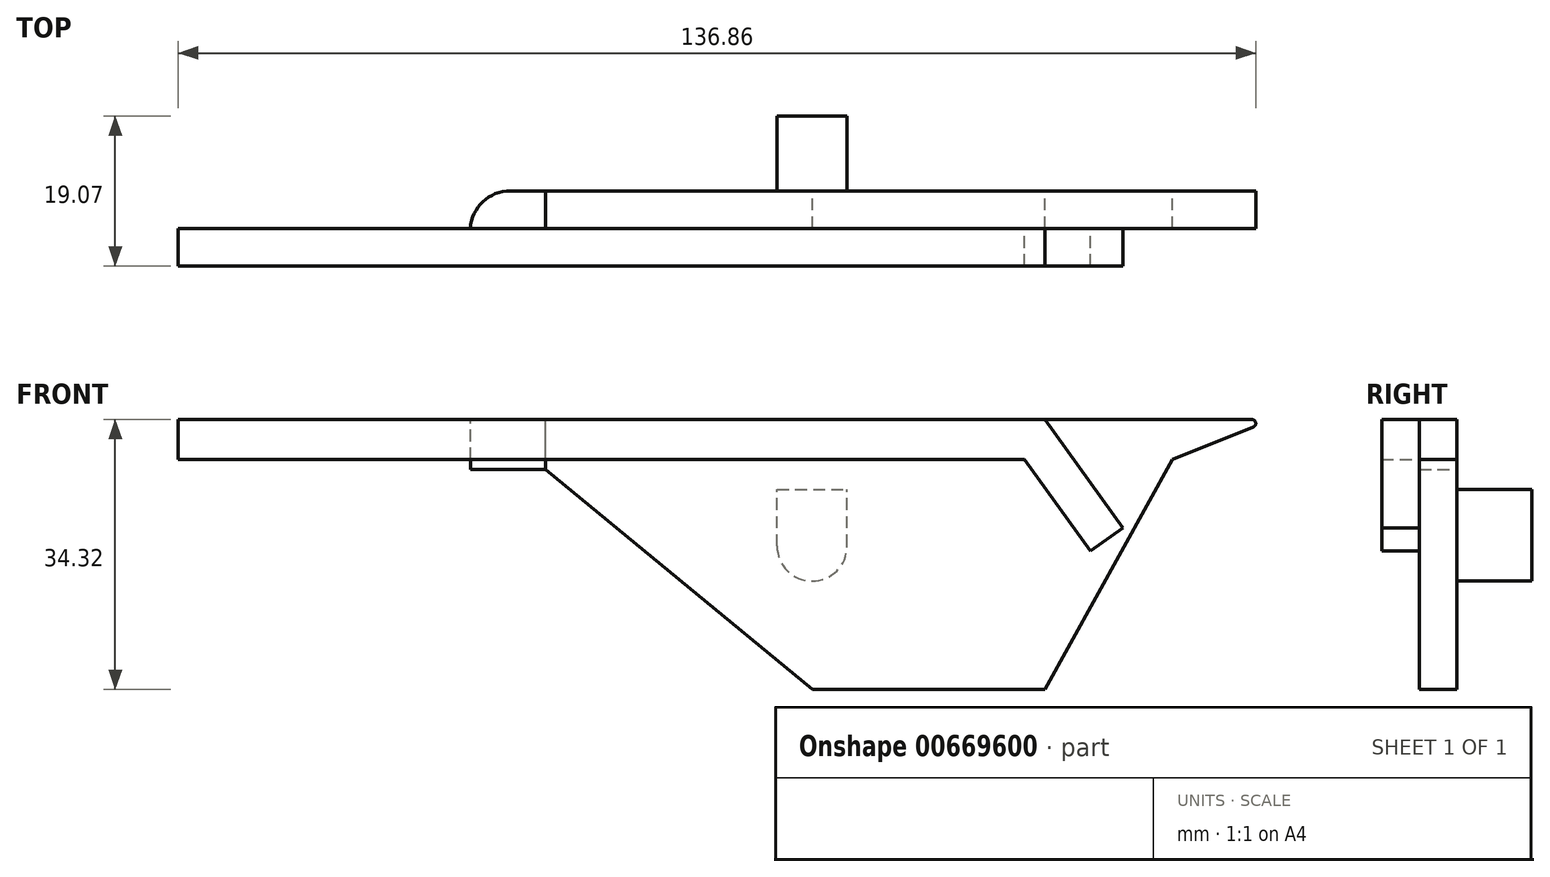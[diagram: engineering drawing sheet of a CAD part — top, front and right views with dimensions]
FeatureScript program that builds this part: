
annotation { "Feature Type Name" : "Feature", "Feature Type Description" : "" }
export const myFeature = defineFeature(function(context is Context, id is Id, definition is map)
    precondition{}
    {
        {
            var Q0;
            Q0=qCreatedBy(makeId("Front.planeOp"),FACE);
            var sketch = newSketch(context, id + "F0", { "sketchPlane" : qUnion([Q0])});
            skLineSegment(sketch, "E0", {"start": v(-28.93, 0) * mm, "end": v(-58.42, 0) * mm});
            skPoint(sketch, "E1.end.orphan", {"position": v(-58.5, 10.16) * mm});
            skPoint(sketch, "E2.end.orphan", {"position": v(-61.98, 10.16) * mm});
            skLineSegment(sketch, "E3", {"start": v(-58.42, 0) * mm, "end": v(-92.38, 27.97) * mm});
            skPoint(sketch, "E4.end.orphan", {"position": v(-68, 0) * mm});
            skLineSegment(sketch, "E5", {"start": v(-92.38, 27.97) * mm, "end": v(-92.38, 34.32) * mm});
            skLineSegment(sketch, "E6", {"start": v(-92.38, 34.32) * mm, "end": v(-28.88, 34.32) * mm});
            skPoint(sketch, "E7.visualSharp", {"position": v(0, 0) * mm});
            skPoint(sketch, "E8.center.orphan", {"position": v(-58.5, 27.97) * mm});
            skLineSegment(sketch, "E9", {"start": v(-2.64, 34.32) * mm, "end": v(-12.73, 34.32) * mm});
            skLineSegment(sketch, "E10", {"start": v(-12.73, 29.24) * mm, "end": v(-2.45, 33.34) * mm});
            skPoint(sketch, "E11.visualSharp", {"position": v(0, 34.32) * mm});
            skArc(sketch, "E11.filletArc", {"start": v(-2.45, 33.34) * mm, "mid": v(-2.14, 33.9) * mm, "end": v(-2.64, 34.32) * mm});
            skLineSegment(sketch, "E12", {"start": v(-28.88, 34.32) * mm, "end": v(-12.73, 34.32) * mm});
            skPoint(sketch, "E13.end.orphan", {"position": v(-12.73, 5.08) * mm});
            skLineSegment(sketch, "E14", {"start": v(-12.73, 29.24) * mm, "end": v(-28.93, 0) * mm});
            skPoint(sketch, "E15.orphan", {"position": v(-20.32, 0) * mm});
            skSolve(sketch);
        }
        {
            var Q0;
            Q0=makeQuery(id+"F0.imprint","IMPRINT",FACE,{"disambiguationData":[TD([[makeQuery(id+"F0.imprint","IMPRINT",EDGE,{"derivedFrom":sQuery(id+"F0.wireOp",EDGE,"E0")}),-1.0]])]});
            extrude(context, id + "F1", {"entities" : qUnion([Q0]), "depth" : 4.76 * mm, "offsetDistance" : 25.4 * mm});
        }
        {
            var Q0;
            Q0=makeQuery(id+"F1.opExtrude","SWEPT_FACE",FACE,{"disambiguationData":[OSD([sQuery(id+"F0.wireOp",EDGE,"E5")])]});
            var sketch = newSketch(context, id + "F2", { "sketchPlane" : qUnion([Q0])});
            skPoint(sketch, "E16.oppositeSnap0", {"position": v(4.76, 31.14) * mm});
            skPoint(sketch, "E16.right.end.orphan", {"position": v(0.07, 31.14) * mm});
            skLineSegment(sketch, "E17.bottom", {"start": v(4.76, 34.32) * mm, "end": v(0, 34.32) * mm});
            skLineSegment(sketch, "E17.top", {"start": v(4.76, 27.97) * mm, "end": v(0, 27.97) * mm});
            skLineSegment(sketch, "E17.left", {"start": v(4.76, 34.32) * mm, "end": v(4.76, 27.97) * mm});
            skLineSegment(sketch, "E17.right", {"start": v(0, 34.32) * mm, "end": v(0, 27.97) * mm});
            skSolve(sketch);
        }
        {
            var Q0;
            Q0=makeQuery(id+"F2.imprint","IMPRINT",FACE,{"disambiguationData":[TD([[makeQuery(id+"F2.imprint","IMPRINT",EDGE,{"derivedFrom":sQuery(id+"F2.wireOp",EDGE,"E17.bottom")}),1.0]])]});
            extrude(context, id + "F3", {"entities" : qUnion([Q0]), "depth" : 9.52 * mm, "offsetDistance" : 25.4 * mm});
        }
        {
            var Q0;
            Q0=makeQuery(id+"F3.opExtrude","CAP_EDGE",EDGE,{"disambiguationData":[OSD([sQuery(id+"F2.wireOp",EDGE,"E17.right")])],"isStart":false});
            fillet(context, id + "F4", {"entities" : qUnion([Q0]), "radius" : 5.08 * mm, "tangentPropagation" : true, "allowEdgeOverflow" : false});
        }
        {
            var Q0;
            Q0=makeQuery(id+"F1.opExtrude","CAP_FACE",FACE,{"disambiguationData":[OSD([sQuery(id+"F0.wireOp",EDGE,"XQ3JfrEa-um1x-yakB-L07f-gmfqccLhQR1l"),sQuery(id+"F0.wireOp",EDGE,"h8YUoyRP-UN5w-zMWy-0Bjt-iXOSloobgran"),sQuery(id+"F0.wireOp",EDGE,"E0"),sQuery(id+"F0.wireOp",EDGE,"E3"),sQuery(id+"F0.wireOp",EDGE,"E5"),sQuery(id+"F0.wireOp",EDGE,"E6"),sQuery(id+"F0.wireOp",EDGE,"SDlrSEQc-8AG4-B69F-MHsA-6caS6OcJrAyO"),sQuery(id+"F0.wireOp",EDGE,"cf4dc3e3-f63d-4539-874e-73eb963e8479"),sQuery(id+"F0.wireOp",EDGE,"E8"),sQuery(id+"F0.wireOp",EDGE,"89Qxk6Pk-JH5j-ieja-Qo85-P2dFUWB4DDen"),sQuery(id+"F0.wireOp",EDGE,"97f87UNE-hL0F-vxin-cXVA-Ms3ejRBOMXvQ"),sQuery(id+"F0.wireOp",EDGE,"E7.filletArc")])],"isStart":true});
            var sketch = newSketch(context, id + "F5", { "sketchPlane" : qUnion([Q0])});
            skArc(sketch, "E18", {"start": v(54.05, 18.23) * mm, "mid": v(58.5, 13.79) * mm, "end": v(62.94, 18.23) * mm});
            skPoint(sketch, "E19.end.orphan", {"position": v(58.5, 13.79) * mm});
            skLineSegment(sketch, "E20", {"start": v(54.05, 18.23) * mm, "end": v(54.05, 25.43) * mm});
            skLineSegment(sketch, "E21", {"start": v(62.94, 18.23) * mm, "end": v(62.94, 25.43) * mm});
            skLineSegment(sketch, "E22", {"start": v(62.94, 25.43) * mm, "end": v(54.05, 25.43) * mm});
            skSolve(sketch);
        }
        {
            var Q0;
            Q0=makeQuery(id+"F5.imprint","IMPRINT",FACE,{"disambiguationData":[TD([[makeQuery(id+"F5.imprint","IMPRINT",EDGE,{"derivedFrom":sQuery(id+"F5.wireOp",EDGE,"E18")}),1.0]])]});
            extrude(context, id + "F6", {"entities" : qUnion([Q0]), "depth" : 9.52 * mm, "offsetDistance" : 25.4 * mm});
        }
        {
            var Q0;
            Q0=makeQuery(id+"F1.opExtrude","CAP_FACE",FACE,{"disambiguationData":[OSD([sQuery(id+"F0.wireOp",EDGE,"E0"),sQuery(id+"F0.wireOp",EDGE,"E3"),sQuery(id+"F0.wireOp",EDGE,"E5"),sQuery(id+"F0.wireOp",EDGE,"E6"),sQuery(id+"F0.wireOp",EDGE,"E9"),sQuery(id+"F0.wireOp",EDGE,"E10"),sQuery(id+"F0.wireOp",EDGE,"E11.filletArc"),sQuery(id+"F0.wireOp",EDGE,"E12"),sQuery(id+"F0.wireOp",EDGE,"E14")])],"isStart":false});
            var sketch = newSketch(context, id + "F7", { "sketchPlane" : qUnion([Q0])});
            skLineSegment(sketch, "E23", {"start": v(-28.93, 0) * mm, "end": v(-28.93, 34.32) * mm});
            skLineSegment(sketch, "E24", {"start": v(-28.93, 34.32) * mm, "end": v(-139, 34.32) * mm});
            skLineSegment(sketch, "E25", {"start": v(-139, 34.32) * mm, "end": v(-139, 29.24) * mm});
            skLineSegment(sketch, "E26", {"start": v(-28.93, 34.32) * mm, "end": v(-19.03, 20.57) * mm});
            skLineSegment(sketch, "E27", {"start": v(-19.03, 20.57) * mm, "end": v(-23.16, 17.6) * mm});
            skLineSegment(sketch, "E28", {"start": v(-139, 29.24) * mm, "end": v(-35.33, 29.24) * mm});
            skLineSegment(sketch, "E29", {"start": v(-23.16, 17.6) * mm, "end": v(-31.53, 29.24) * mm});
            skLineSegment(sketch, "E30", {"start": v(-35.33, 29.24) * mm, "end": v(-31.53, 29.24) * mm});
            skSolve(sketch);
        }
        {
            var Q0;
            Q0 = qSketchRegion(id + "F7", true);
            extrude(context, id + "F8", {"entities" : qUnion([Q0]), "depth" : 4.78 * mm, "offsetDistance" : 25.4 * mm});
        }
    });
